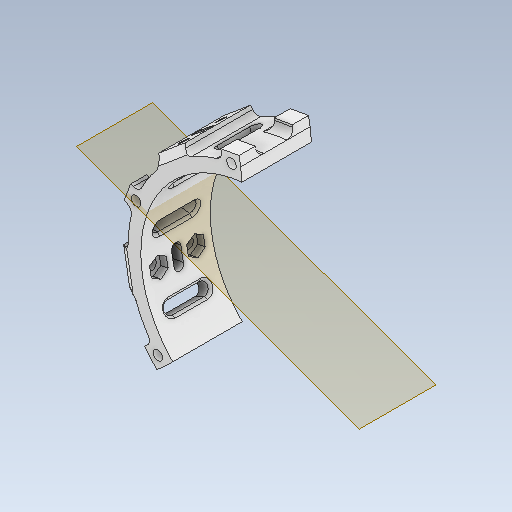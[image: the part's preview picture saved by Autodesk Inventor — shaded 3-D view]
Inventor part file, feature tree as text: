
AUTODESK INVENTOR PART (.ipt)
format: ipt  version: 2020 (Build 240168000, 168)  size: 623,104 bytes
history: native  units: mm
features: extrude x10, sketch x10, projected_geometry x9, plane x5, pattern_circular x4, reference x4, other x4, mirror x3, chamfer x3, fillet x2, shell x1
ambient origin geometry x8: Origin, YZ Plane, XZ Plane, XY Plane, X Axis, Y Axis, Z Axis, Center Point
bodies: Solid1 (feature_tree)
feature tree (55):
  extrude  "Extrusion1"  Depth=108.0mm
  extrude  "Extrusion2"  Depth=3.490659mm
  plane  "Work Plane1"
  mirror  "Mirror1"
  extrude  "Extrusion3"  Depth=15.0mm
  pattern_circular  "Circular Pattern1"  Count=4 Angle=180.0deg
  extrude  "Extrusion4"  Depth=50.0mm TaperAngle=0.0deg
  pattern_circular  "Circular Pattern2"  Count=3 Angle=120.0deg
  plane  "Work Plane2"
  mirror  "Mirror2"
  plane  "Work Plane3"
  extrude  "Extrusion5"  Depth=4.1mm
  extrude  "Extrusion6"  Depth=5.0mm TaperAngle=0.0deg
  pattern_circular  "Circular Pattern3"  Count=3 Angle=120.0deg
  extrude  "Extrusion7"  [1 undecoded]
  extrude  "Extrusion8"  Depth=7.0mm
  pattern_circular  "Circular Pattern4"  [2 undecoded]
  fillet  "Fillet1"  Radius=4.1mm
  fillet  "Fillet2"  Radius=4.1mm
  chamfer  "Chamfer1"  Distance=15.0mm
  chamfer  "Chamfer2"  Distance=4.2mm
  plane  "Work Plane4"
  extrude  "Extrusion9"  Depth=60.0mm TaperAngle=360.0deg
  plane  "Work Plane5"
  extrude  "Extrusion10"  Depth=4.2mm
  mirror  "Mirror3"
  chamfer  "Chamfer3"  Distance=60.0mm Angle=360.0deg
  sketch  "Sketch1"  dims[d0=97.0mm d1=108.0mm]
  reference  "Reference1"
  reference  "Reference2"
  reference  "Reference3"
  reference  "Reference4"
  sketch  "Sketch2"  dims[d2=54.0mm d3=3.490659mm]
  projected_geometry  "Projected Loop1"
  sketch  "Sketch3"  dims[d4=0.0mm d5=15.0mm]
  projected_geometry  "Projected Loop2"
  sketch  "Sketch4"  dims[d6=7.0mm d7=40.0mm d9=180.0deg]
  projected_geometry  "Projected Loop3"
  sketch  "Sketch5"  dims[d11=30.0mm d12=0.0mm d13=50.0mm d14=0.0mm]
  projected_geometry  "Projected Loop4"
  sketch  "Sketch6"  dims[d15=4.0mm]
  projected_geometry  "Projected Loop5"
  sketch  "Sketch7"  dims[d16=8.0mm]
  projected_geometry  "Projected Loop6"
  sketch  "Sketch8"  dims[d17=8.0mm]
  sketch  "Sketch9"  dims[d18=7.0mm d19=0.0mm d20=30.0mm d21=120.0deg]
  projected_geometry  "Projected Loop7"
  sketch  "Sketch10"  dims[d23=4.0mm d24=4.1mm d25=5.0mm d26=0.0mm d27=30.0mm d28=120.0deg d30=-10.0mm d31=7.0mm d32=7.0mm d33=4.1mm d34=4.1mm d35=15.0mm d36=0.0mm d37=4.2mm d38=60.0mm d40=360.0deg d42=4.2mm d43=60.0mm d45=360.0deg d47=4.2mm d48=0.0mm d49=40.0mm d50=180.0deg d52=4.2mm d53=0.0mm d54=3.0mm d55=4.0mm d56=10.0mm d57=0.0mm d58=20.0mm d59=60.0deg d61=3.0mm d62=3.0mm d63=2.0mm d64=2.0mm d65=60.0deg d66=2.0mm d67=2.0mm d68=60.0deg d69=7.0mm d70=5.0mm d71=10.0mm d72=0.0mm d73=7.0mm d74=5.0mm d75=10.0mm d76=0.0mm d77=1.0mm d78=2.0mm d79=60.0deg]
  projected_geometry  "Projected Loop8"
  projected_geometry  "Projected Loop9"
  parser-record x1  (decoder bookkeeping rows leaked as tree rows — omitted from the tree; the rows remain in map.json)
  other  "reducer_2.iam"
  shell  "shell_2:1"  Thickness=4.2mm
  other  "90_motor:1"
  other  "90motor_top:1"
note: 3 required parameter values undecoded (feature->parameter linkage not recoverable at this tier; creation-order binding heuristic only, values carry confidence <= 0.55)
note: 1 file-system path scrubbed to <path> (originals preserved in map.json)
